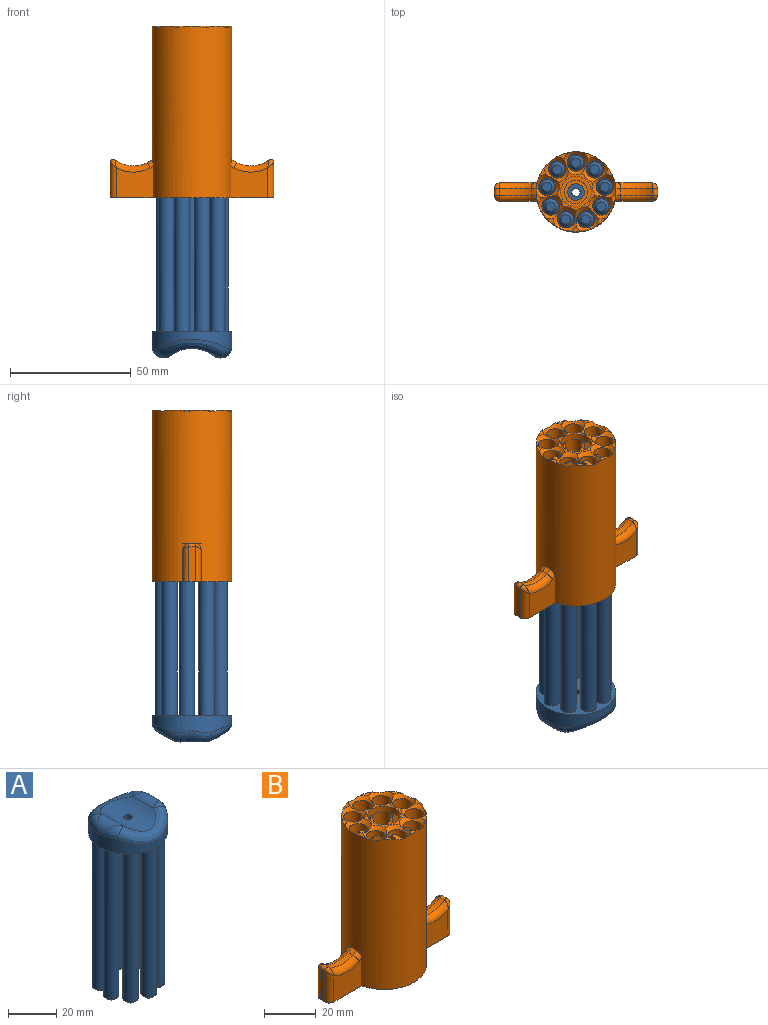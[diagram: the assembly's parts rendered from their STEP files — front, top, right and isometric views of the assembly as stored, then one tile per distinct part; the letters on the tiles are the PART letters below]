
ASSEMBLY  parts=2 mates=1
PART A: 39 faces, bbox 33x33.1x92.5 mm
  f0: cylinder r=4.76mm len=12.06mm, axis (0,1,0), area 72mm2, adj f1,f35,f38
  f1: cylinder r=14.82mm len=25.4mm, axis (0,1,0), area 397.2mm2, adj f0,f2,f32,f34,f37
  f2: cylinder r=4.76mm len=12.06mm, axis (0,1,0), area 72mm2, adj f1,f33,f36
  f3: plane 33.02x33.02mm, normal (0,0,-1), area 562.1mm2, adj f4,f5,f7,f9,f11,f13,f15,f17
  f4: cylinder r=16.51mm len=33.02mm, axis (0,0,-1), area 561.1mm2, adj f3,f33,f34,f35,f36,f37,f38
  f5: cylinder r=3.17mm len=75.95mm, axis (0,0,1), area 1515.1mm2, adj f3,f30
  f6: plane 3.81x3.81mm, normal (0,0,-1), area 11.4mm2, adj f30
  f7: cylinder r=3.17mm len=75.95mm, axis (0,0,1), area 1515.1mm2, adj f3,f31
  f8: plane 3.81x3.81mm, normal (0,0,-1), area 11.4mm2, adj f31
  f9: cylinder r=3.17mm len=75.95mm, axis (0,0,1), area 1515.1mm2, adj f3,f24
  f10: plane 3.81x3.81mm, normal (0,0,-1), area 11.4mm2, adj f24
  f11: cylinder r=3.17mm len=75.95mm, axis (0,0,1), area 1515.1mm2, adj f3,f25
  f12: plane 3.81x3.81mm, normal (0,0,-1), area 11.4mm2, adj f25
  f13: cylinder r=3.17mm len=75.95mm, axis (0,0,1), area 1515.1mm2, adj f3,f23
  f14: plane 3.81x3.81mm, normal (0,0,-1), area 11.4mm2, adj f23
  f15: cylinder r=3.17mm len=75.95mm, axis (0,0,1), area 1515.1mm2, adj f3,f26
  f16: plane 3.81x3.81mm, normal (0,0,-1), area 11.4mm2, adj f26
  f17: cylinder r=3.17mm len=75.95mm, axis (0,0,1), area 1515.1mm2, adj f3,f27
  f18: plane 3.81x3.81mm, normal (0,0,-1), area 11.4mm2, adj f27
  f19: cylinder r=3.17mm len=75.95mm, axis (0,0,1), area 1515.1mm2, adj f3,f28
  f20: plane 3.81x3.81mm, normal (0,0,-1), area 11.4mm2, adj f28
  f21: cylinder r=3.17mm len=75.95mm, axis (0,0,1), area 1515.1mm2, adj f3,f29
  f22: plane 3.81x3.81mm, normal (0,0,-1), area 11.4mm2, adj f29
  f23: cone r=1.91mm half-angle=45deg, axis (0,0,1), area 28.7mm2, adj f13,f14
  f24: cone r=1.91mm half-angle=45deg, axis (0,0,1), area 28.7mm2, adj f9,f10
  f25: cone r=1.91mm half-angle=45deg, axis (0,0,1), area 28.7mm2, adj f11,f12
  f26: cone r=1.91mm half-angle=45deg, axis (0,0,1), area 28.7mm2, adj f15,f16
  f27: cone r=1.91mm half-angle=45deg, axis (0,0,1), area 28.7mm2, adj f17,f18
  f28: cone r=1.91mm half-angle=45deg, axis (0,0,1), area 28.7mm2, adj f19,f20
  f29: cone r=1.91mm half-angle=45deg, axis (0,0,1), area 28.7mm2, adj f21,f22
  f30: cone r=1.91mm half-angle=45deg, axis (0,0,1), area 28.7mm2, adj f5,f6
  f31: cone r=1.91mm half-angle=45deg, axis (0,0,1), area 28.7mm2, adj f7,f8
  f32: cylinder r=1.71mm len=7.3mm, axis (0,0,-1), area 78.6mm2, adj f1,f3
  f33: bspline ~10.95x8.11mm, area 37.6mm2, adj f2,f4,f34
  f34: bspline ~30.37x11.53mm, area 212.7mm2, adj f1,f4,f33,f35
  f35: bspline ~10.95x8.11mm, area 37.6mm2, adj f0,f4,f34
  f36: bspline ~10.95x8.11mm, area 37.6mm2, adj f2,f4,f37
  f37: bspline ~31.45x12.61mm, area 212.7mm2, adj f1,f4,f36,f38
  f38: bspline ~10.95x8.11mm, area 37.6mm2, adj f0,f4,f37
PART B: 85 faces, bbox 70.5x33.8x71.2 mm
  f0: cylinder r=16.51mm len=71.12mm, axis (0,0,-1), area 7035.7mm2, adj f3,f4,f5,f8,f9,f10,f11,f12
  f1: cylinder r=3.62mm len=69.6mm, axis (0,0,-1), area 1450.6mm2, adj f26,f29,f32,f39,f41,f49,f77,f78
  f2: plane 9.65x9.65mm, normal (0,0,1), area 36.2mm2, adj f28,f76
  f3: plane 15.24x13.02mm, normal (0,-1,0), area 172.7mm2, adj f0,f26,f72,f73,f75
  f4: plane 15.24x13.02mm, normal (0,1,0), area 172.7mm2, adj f0,f26,f60,f62,f63
  f5: plane 15.24x13.02mm, normal (0,1,0), area 172.7mm2, adj f0,f26,f68,f69,f71
  f6: plane 14.61x2.54mm, normal (1,0,0), area 37.1mm2, adj f26,f58,f71,f75
  f7: plane 14.61x2.54mm, normal (-1,0,0), area 37.1mm2, adj f26,f54,f60,f64
  f8: plane 4.97x2.66mm, normal (0,0,1), area 4.6mm2, adj f0,f49,f50
  f9: plane 4.97x2.66mm, normal (0,0,1), area 4.6mm2, adj f0,f47,f49
  f10: plane 4.58x2.94mm, normal (0,0,1), area 4.6mm2, adj f0,f45,f47
  f11: plane 5.21x2.3mm, normal (0,0,1), area 4.6mm2, adj f0,f43,f45
  f12: plane 4.05x3.4mm, normal (0,0,1), area 4.6mm2, adj f0,f42,f43
  f13: plane 5.29x2.08mm, normal (0,0,1), area 4.6mm2, adj f0,f42,f44
  f14: plane 4.05x3.4mm, normal (0,0,1), area 4.6mm2, adj f0,f44,f46
  f15: plane 16.39x16.14mm, normal (0,0,1), area 43.8mm2, adj f27,f42,f43,f44,f45,f46,f47,f48
  f16: plane 4.58x2.94mm, normal (0,0,1), area 4.6mm2, adj f0,f48,f50
  f17: cylinder r=3.62mm len=69.6mm, axis (0,0,-1), area 1529mm2, adj f26,f29,f30,f39,f41,f47
  f18: cylinder r=3.62mm len=69.6mm, axis (0,0,-1), area 1529mm2, adj f26,f30,f31,f39,f41,f45
  f19: cylinder r=3.62mm len=69.6mm, axis (0,0,-1), area 1529.1mm2, adj f26,f31,f33,f39,f41,f43
  f20: cylinder r=3.62mm len=69.6mm, axis (0,0,-1), area 1529.2mm2, adj f26,f33,f34,f39,f41,f42
  f21: cylinder r=3.62mm len=69.6mm, axis (0,0,-1), area 1529mm2, adj f26,f34,f39,f40,f41,f44
  f22: cylinder r=3.62mm len=69.6mm, axis (0,0,-1), area 1529mm2, adj f26,f35,f39,f40,f41,f46
  f23: cylinder r=3.62mm len=69.6mm, axis (0,0,-1), area 1529.1mm2, adj f26,f35,f36,f39,f41,f48
  f24: cylinder r=3.62mm len=69.6mm, axis (0,0,-1), area 1529mm2, adj f26,f32,f36,f39,f41,f50
  f25: plane 5.21x2.3mm, normal (0,0,1), area 4.6mm2, adj f0,f46,f48
  f26: plane 67.69x33.02mm, normal (0,0,-1), area 709.9mm2, adj f0,f1,f3,f4,f5,f6,f7,f17
  f27: cylinder r=6.35mm len=12.7mm, axis (0,0,1), area 111.5mm2, adj f15,f37
  f28: cylinder r=3.43mm len=6.86mm, axis (0,0,1), area 27.4mm2, adj f2,f26
  f29: torus R=8.72mm, axis (0,0,1), area 5.5mm2, adj f1,f17,f39,f41
  f30: torus R=8.72mm, axis (0,0,1), area 5.5mm2, adj f17,f18,f39,f41
  f31: torus R=8.72mm, axis (0,0,1), area 5.5mm2, adj f18,f19,f39,f41
  f32: torus R=8.72mm, axis (0,0,1), area 5.5mm2, adj f1,f24,f39,f41
  f33: torus R=8.72mm, axis (0,0,1), area 5.5mm2, adj f19,f20,f39,f41
  f34: torus R=8.72mm, axis (0,0,1), area 5.6mm2, adj f20,f21,f39,f41
  f35: torus R=8.72mm, axis (0,0,1), area 5.5mm2, adj f22,f23,f39,f41
  f36: torus R=8.72mm, axis (0,0,1), area 5.5mm2, adj f23,f24,f39,f41
  f37: plane 14.67x14.67mm, normal (0,0,-1), area 42.2mm2, adj f27,f41
  f38: plane 14.67x14.67mm, normal (0,0,1), area 95.7mm2, adj f39,f76
  f39: cone r=7.33mm half-angle=51.1deg, axis (0,0,1), area 131.7mm2, adj f1,f17,f18,f19,f20,f21,f22,f23
  f40: torus R=8.72mm, axis (0,0,1), area 5.5mm2, adj f21,f22,f39,f41
  f41: cone r=7.33mm half-angle=51.1deg, axis (0,0,-1), area 131.8mm2, adj f1,f17,f18,f19,f20,f21,f22,f23
  f42: cone r=3.62mm half-angle=45deg, axis (0,0,1), area 43.1mm2, adj f0,f12,f13,f15,f20,f43,f44
  f43: cone r=3.62mm half-angle=45deg, axis (0,0,1), area 43.1mm2, adj f0,f11,f12,f15,f19,f42,f45
  f44: cone r=3.62mm half-angle=45deg, axis (0,0,1), area 43.1mm2, adj f0,f13,f14,f15,f21,f42,f46
  f45: cone r=3.62mm half-angle=45deg, axis (0,0,1), area 43.1mm2, adj f0,f10,f11,f15,f18,f43,f47
  f46: cone r=3.62mm half-angle=45deg, axis (0,0,1), area 43.1mm2, adj f0,f14,f15,f22,f25,f44,f48
  f47: cone r=3.62mm half-angle=45deg, axis (0,0,1), area 43.2mm2, adj f0,f9,f10,f15,f17,f45,f49
  f48: cone r=3.62mm half-angle=45deg, axis (0,0,1), area 43.4mm2, adj f0,f15,f16,f23,f25,f46,f50
  f49: cone r=3.62mm half-angle=45deg, axis (0,0,1), area 43.3mm2, adj f0,f1,f8,f9,f15,f47,f50
  f50: cone r=3.62mm half-angle=45deg, axis (0,0,1), area 43.2mm2, adj f0,f8,f15,f16,f24,f48,f49
  f51: plane 15.24x13.02mm, normal (0,-1,0), area 172.7mm2, adj f0,f26,f64,f66,f67
  f52: plane 7.62x0.45mm, normal (0,0,-1), area 2.3mm2, adj f0,f55
  f53: cylinder r=12.7mm len=13.3mm, axis (0,-1,0), area 35.7mm2, adj f54,f55,f62,f66
  f54: cylinder r=1.27mm len=2.54mm, axis (0,-1,0), area 7.1mm2, adj f7,f53,f61,f65
  f55: plane 7.67x2.52mm, normal (-0.46,0,0.89), area 8.4mm2, adj f0,f52,f53,f63,f67
  f56: plane 7.62x0.45mm, normal (0,0,-1), area 2.3mm2, adj f0,f59
  f57: cylinder r=12.7mm len=13.3mm, axis (0,-1,0), area 35.7mm2, adj f58,f59,f69,f73
  f58: cylinder r=1.27mm len=2.54mm, axis (0,-1,0), area 7.1mm2, adj f6,f57,f70,f74
  f59: plane 7.67x2.52mm, normal (0.46,0,0.89), area 8.4mm2, adj f0,f56,f57,f68,f72
  f60: cylinder r=2.54mm len=14.61mm, axis (0,0,-1), area 54.9mm2, adj f4,f7,f26,f61
  f61: bspline ~4.77x3.42mm, area 8mm2, adj f54,f60,f62
  f62: torus R=15.24mm, axis (0,-1,0), area 56.7mm2, adj f4,f53,f61,f63
  f63: cylinder r=2.54mm len=3.34mm, axis (0.89,0,0.46), area 8.4mm2, adj f0,f4,f55,f62
  f64: cylinder r=2.54mm len=14.61mm, axis (0,0,-1), area 54.9mm2, adj f7,f26,f51,f65
  f65: bspline ~4.77x3.42mm, area 8mm2, adj f54,f64,f66
  f66: torus R=15.24mm, axis (0,1,0), area 56.7mm2, adj f51,f53,f65,f67
  f67: cylinder r=2.54mm len=3.34mm, axis (0.89,0,0.46), area 8.4mm2, adj f0,f51,f55,f66
  f68: cylinder r=2.54mm len=3.34mm, axis (0.89,0,-0.46), area 8.4mm2, adj f0,f5,f59,f69
  f69: torus R=15.24mm, axis (0,1,0), area 56.7mm2, adj f5,f57,f68,f70
  f70: bspline ~4.77x3.42mm, area 8mm2, adj f58,f69,f71
  f71: cylinder r=2.54mm len=14.61mm, axis (0,0,-1), area 54.9mm2, adj f5,f6,f26,f70
  f72: cylinder r=2.54mm len=3.34mm, axis (-0.89,0,0.46), area 8.4mm2, adj f0,f3,f59,f73
  f73: torus R=15.24mm, axis (0,-1,0), area 56.7mm2, adj f3,f57,f72,f74
  f74: bspline ~4.77x3.42mm, area 8mm2, adj f58,f73,f75
  f75: cylinder r=2.54mm len=14.61mm, axis (0,0,-1), area 54.9mm2, adj f3,f6,f26,f74
  f76: cylinder r=4.83mm len=57.41mm, axis (0,0,1), area 1740.7mm2, adj f2,f38
  f77: plane 2.03x0.93mm, normal (0,0,1), area 1.7mm2, adj f0,f1,f78,f79
  f78: plane 19.05x0.9mm, normal (-1,0,0), area 17.1mm2, adj f0,f1,f77,f80
  f79: plane 19.05x0.9mm, normal (1,0,0), area 17.1mm2, adj f0,f1,f77,f80
  f80: plane 2.03x0.93mm, normal (0,0,-1), area 1.7mm2, adj f0,f1,f78,f79
  f81: plane 19.05x0.9mm, normal (1,0,0), area 17.1mm2, adj f0,f1,f82,f83
  f82: plane 2.03x0.93mm, normal (0,0,1), area 1.7mm2, adj f0,f1,f81,f84
  f83: plane 2.03x0.93mm, normal (0,0,-1), area 1.7mm2, adj f0,f1,f81,f84
  f84: plane 19.05x0.9mm, normal (-1,0,0), area 17.1mm2, adj f0,f1,f82,f83
PLACE A rot(axis=(1,0,0),180deg) t=(-29.11,-26.9,-80.41)mm
PLACE B t=(-29.11,-26.9,-25.3)mm fixed
MATE slider A.f4 <-> B.f0  axis (0,0,1) through (-29.11,-26.9,-84.1)mm
